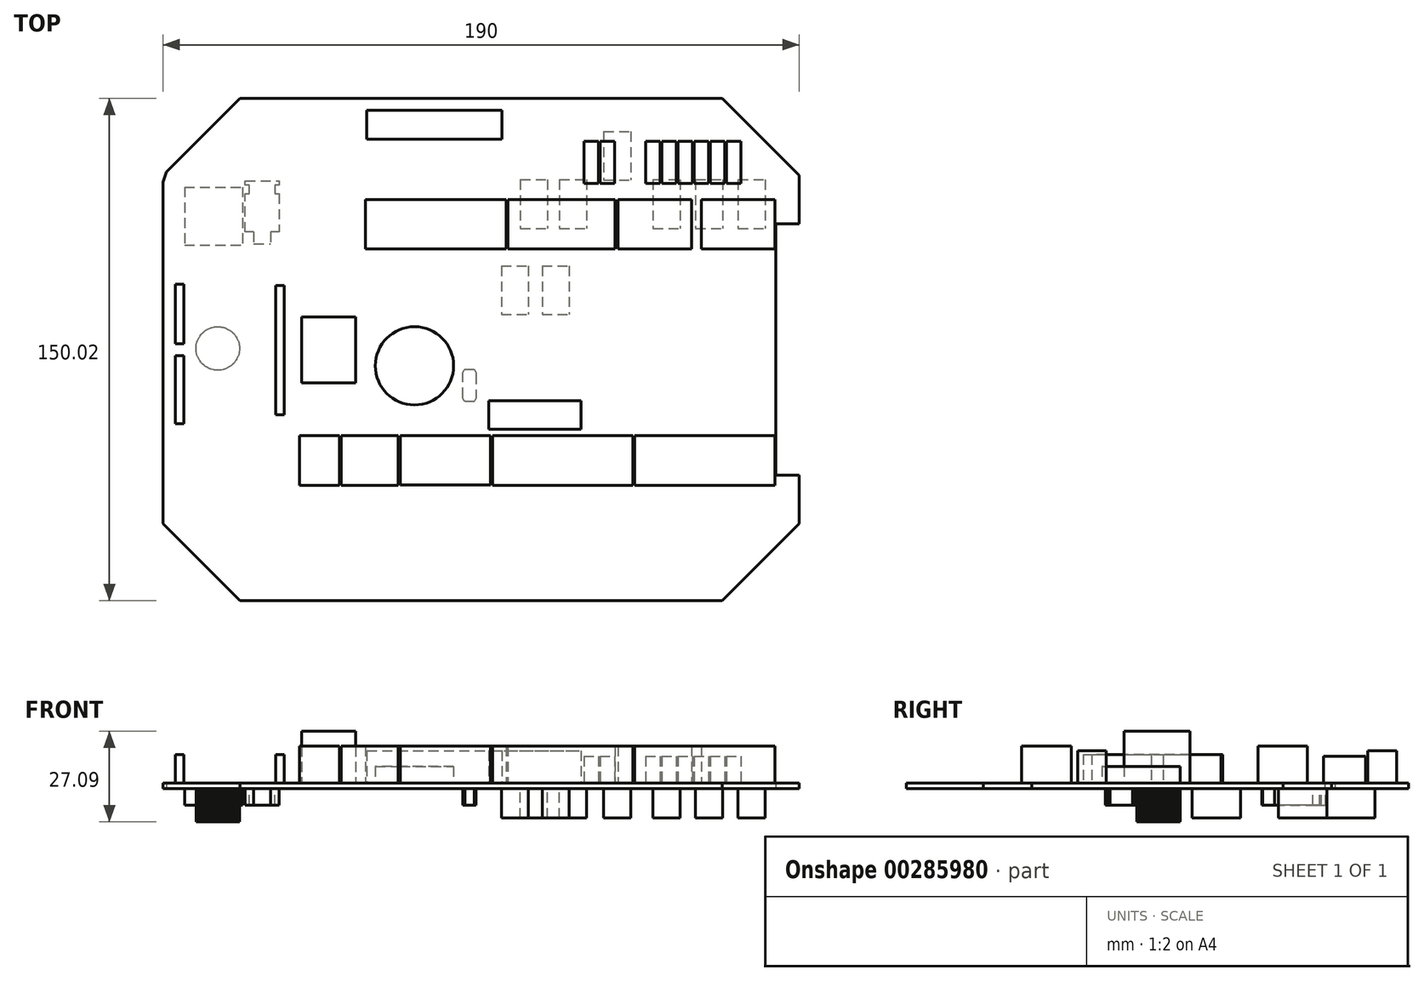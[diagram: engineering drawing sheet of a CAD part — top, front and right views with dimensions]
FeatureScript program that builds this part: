
annotation { "Feature Type Name" : "Feature", "Feature Type Description" : "" }
export const myFeature = defineFeature(function(context is Context, id is Id, definition is map)
    precondition{}
    {
        {
            var Q0;
            Q0=qCreatedBy(makeId("Top.planeOp"),FACE);
            var sketch = newSketch(context, id + "F0", { "sketchPlane" : qUnion([Q0])});
            skLineSegment(sketch, "E0", {"start": v(-92.96, -47) * mm, "end": v(-92.7, -46.96) * mm});
            skLineSegment(sketch, "E1", {"start": v(-92.7, -46.96) * mm, "end": v(-92.46, -46.91) * mm});
            skLineSegment(sketch, "E2", {"start": v(-92.46, -46.91) * mm, "end": v(-92.23, -46.81) * mm});
            skLineSegment(sketch, "E3", {"start": v(-92.23, -46.81) * mm, "end": v(-92.02, -46.69) * mm});
            skLineSegment(sketch, "E4", {"start": v(-92.02, -46.69) * mm, "end": v(-91.85, -46.5) * mm});
            skLineSegment(sketch, "E5", {"start": v(-91.85, -46.5) * mm, "end": v(-91.7, -46.33) * mm});
            skLineSegment(sketch, "E6", {"start": v(-91.7, -46.33) * mm, "end": v(-91.5, -45.87) * mm});
            skLineSegment(sketch, "E7", {"start": v(-91.5, -45.87) * mm, "end": v(-91.47, -45.62) * mm});
            skLineSegment(sketch, "E8", {"start": v(-91.47, -45.62) * mm, "end": v(-91.47, -45.36) * mm});
            skLineSegment(sketch, "E9", {"start": v(-91.47, -45.36) * mm, "end": v(-91.5, -45.14) * mm});
            skLineSegment(sketch, "E10", {"start": v(-91.5, -45.14) * mm, "end": v(-91.6, -44.88) * mm});
            skLineSegment(sketch, "E11", {"start": v(-91.6, -44.88) * mm, "end": v(-91.7, -44.68) * mm});
            skLineSegment(sketch, "E12", {"start": v(-91.7, -44.68) * mm, "end": v(-91.85, -44.5) * mm});
            skLineSegment(sketch, "E13", {"start": v(-91.85, -44.5) * mm, "end": v(-92.02, -44.32) * mm});
            skLineSegment(sketch, "E14", {"start": v(-92.02, -44.32) * mm, "end": v(-92.23, -44.17) * mm});
            skLineSegment(sketch, "E15", {"start": v(-92.23, -44.17) * mm, "end": v(-92.46, -44.1) * mm});
            skLineSegment(sketch, "E16", {"start": v(-92.46, -44.1) * mm, "end": v(-92.7, -44.02) * mm});
            skLineSegment(sketch, "E17", {"start": v(-92.7, -44.02) * mm, "end": v(-92.96, -44) * mm});
            skLineSegment(sketch, "E18", {"start": v(-92.68, 50.01) * mm, "end": v(-92.46, 50.09) * mm});
            skLineSegment(sketch, "E19", {"start": v(-92.46, 50.09) * mm, "end": v(-92.2, 50.2) * mm});
            skLineSegment(sketch, "E20", {"start": v(-92.2, 50.2) * mm, "end": v(-92, 50.37) * mm});
            skLineSegment(sketch, "E21", {"start": v(-92, 50.37) * mm, "end": v(-91.82, 50.52) * mm});
            skLineSegment(sketch, "E22", {"start": v(-91.82, 50.52) * mm, "end": v(-91.64, 50.75) * mm});
            skLineSegment(sketch, "E23", {"start": v(-91.64, 50.75) * mm, "end": v(-91.54, 50.98) * mm});
            skLineSegment(sketch, "E24", {"start": v(-91.54, 50.98) * mm, "end": v(-91.47, 51.23) * mm});
            skLineSegment(sketch, "E25", {"start": v(-91.47, 51.23) * mm, "end": v(-91.47, 51.74) * mm});
            skLineSegment(sketch, "E26", {"start": v(-91.47, 51.74) * mm, "end": v(-91.54, 52) * mm});
            skLineSegment(sketch, "E27", {"start": v(-91.54, 52) * mm, "end": v(-91.64, 52.25) * mm});
            skLineSegment(sketch, "E28", {"start": v(-91.64, 52.25) * mm, "end": v(-91.8, 52.45) * mm});
            skLineSegment(sketch, "E29", {"start": v(-91.8, 52.45) * mm, "end": v(-91.97, 52.65) * mm});
            skLineSegment(sketch, "E30", {"start": v(-91.97, 52.65) * mm, "end": v(-92.18, 52.78) * mm});
            skLineSegment(sketch, "E31", {"start": v(-92.18, 52.78) * mm, "end": v(-92.43, 52.9) * mm});
            skLineSegment(sketch, "E32", {"start": v(-92.43, 52.9) * mm, "end": v(-92.68, 52.98) * mm});
            skLineSegment(sketch, "E33", {"start": v(88.01, -37.5) * mm, "end": v(88.01, 37.5) * mm});
            skLineSegment(sketch, "E34", {"start": v(-95, -47) * mm, "end": v(-92.96, -47) * mm});
            skLineSegment(sketch, "E35", {"start": v(-95, 50.01) * mm, "end": v(-92.68, 50.01) * mm});
            skLineSegment(sketch, "E36", {"start": v(-72, 75) * mm, "end": v(72, 75) * mm});
            skLineSegment(sketch, "E37", {"start": v(-72, -75) * mm, "end": v(72, -75) * mm});
            skLineSegment(sketch, "E38", {"start": v(-95, -52) * mm, "end": v(-72, -75) * mm});
            skLineSegment(sketch, "E39", {"start": v(95, 37.5) * mm, "end": v(95, 52) * mm});
            skLineSegment(sketch, "E40", {"start": v(95, -52) * mm, "end": v(95, -37.5) * mm});
            skLineSegment(sketch, "E41", {"start": v(72, 75) * mm, "end": v(95, 52) * mm});
            skLineSegment(sketch, "E42", {"start": v(72, -75) * mm, "end": v(95, -52) * mm});
            skLineSegment(sketch, "E43", {"start": v(88.01, 37.5) * mm, "end": v(95, 37.5) * mm});
            skLineSegment(sketch, "E44", {"start": v(88.01, -37.5) * mm, "end": v(95, -37.5) * mm});
            skLineSegment(sketch, "E45", {"start": v(-93.2, 52.98) * mm, "end": v(-92.68, 52.98) * mm});
            skLineSegment(sketch, "E46", {"start": v(-94, 53) * mm, "end": v(-72, 75) * mm});
            skLineSegment(sketch, "E47", {"start": v(-94, 53) * mm, "end": v(-93.22, 53) * mm});
            skLineSegment(sketch, "E48", {"start": v(-95, -44) * mm, "end": v(-92.96, -44) * mm});
            skLineSegment(sketch, "E49", {"start": v(-95, -52) * mm, "end": v(-95, 50.01) * mm});
            skLineSegment(sketch, "E50", {"start": v(-95, 50.01) * mm, "end": v(-94, 53) * mm});
            skSolve(sketch);
        }
        {
            var Q0;
            Q0 = qSketchRegion(id + "F0", true);
            extrude(context, id + "F1", {"entities" : qUnion([Q0]), "depth" : 1.6 * mm});
        }
        {
            var Q0;
            Q0=makeQuery(id+"F1.opExtrude","CAP_FACE",FACE,{"disambiguationData":[OSD([sQuery(id+"F0.wireOp",EDGE,"E33"),sQuery(id+"F0.wireOp",EDGE,"E36"),sQuery(id+"F0.wireOp",EDGE,"E37"),sQuery(id+"F0.wireOp",EDGE,"E38"),sQuery(id+"F0.wireOp",EDGE,"E39"),sQuery(id+"F0.wireOp",EDGE,"E40"),sQuery(id+"F0.wireOp",EDGE,"E41"),sQuery(id+"F0.wireOp",EDGE,"E42"),sQuery(id+"F0.wireOp",EDGE,"E43"),sQuery(id+"F0.wireOp",EDGE,"E44"),sQuery(id+"F0.wireOp",EDGE,"E46"),sQuery(id+"F0.wireOp",EDGE,"E49"),sQuery(id+"F0.wireOp",EDGE,"E50")])],"isStart":false});
            var sketch = newSketch(context, id + "F2", { "sketchPlane" : qUnion([Q0])});
            skLineSegment(sketch, "E51", {"start": v(-92.96, -47) * mm, "end": v(-92.7, -46.96) * mm});
            skLineSegment(sketch, "E52", {"start": v(-92.7, -46.96) * mm, "end": v(-92.46, -46.91) * mm});
            skLineSegment(sketch, "E53", {"start": v(-92.46, -46.91) * mm, "end": v(-92.23, -46.81) * mm});
            skLineSegment(sketch, "E54", {"start": v(-92.23, -46.81) * mm, "end": v(-92.02, -46.69) * mm});
            skLineSegment(sketch, "E55", {"start": v(-92.02, -46.69) * mm, "end": v(-91.85, -46.5) * mm});
            skLineSegment(sketch, "E56", {"start": v(-91.85, -46.5) * mm, "end": v(-91.7, -46.33) * mm});
            skLineSegment(sketch, "E57", {"start": v(-91.7, -46.33) * mm, "end": v(-91.6, -46.1) * mm});
            skLineSegment(sketch, "E58", {"start": v(-91.6, -46.1) * mm, "end": v(-91.5, -45.87) * mm});
            skLineSegment(sketch, "E59", {"start": v(-91.5, -45.87) * mm, "end": v(-91.47, -45.62) * mm});
            skLineSegment(sketch, "E60", {"start": v(-91.47, -45.62) * mm, "end": v(-91.47, -45.36) * mm});
            skLineSegment(sketch, "E61", {"start": v(-91.47, -45.36) * mm, "end": v(-91.5, -45.14) * mm});
            skLineSegment(sketch, "E62", {"start": v(-91.5, -45.14) * mm, "end": v(-91.6, -44.88) * mm});
            skLineSegment(sketch, "E63", {"start": v(-91.6, -44.88) * mm, "end": v(-91.7, -44.68) * mm});
            skLineSegment(sketch, "E64", {"start": v(-91.7, -44.68) * mm, "end": v(-91.85, -44.5) * mm});
            skLineSegment(sketch, "E65", {"start": v(-91.85, -44.5) * mm, "end": v(-92.02, -44.32) * mm});
            skLineSegment(sketch, "E66", {"start": v(-92.02, -44.32) * mm, "end": v(-92.23, -44.17) * mm});
            skLineSegment(sketch, "E67", {"start": v(-92.23, -44.17) * mm, "end": v(-92.46, -44.1) * mm});
            skLineSegment(sketch, "E68", {"start": v(-92.46, -44.1) * mm, "end": v(-92.7, -44.02) * mm});
            skLineSegment(sketch, "E69", {"start": v(-92.7, -44.02) * mm, "end": v(-92.96, -44) * mm});
            skLineSegment(sketch, "E70", {"start": v(-92.96, 50.01) * mm, "end": v(-92.68, 50.01) * mm});
            skLineSegment(sketch, "E71", {"start": v(-92.68, 50.01) * mm, "end": v(-92.46, 50.09) * mm});
            skLineSegment(sketch, "E72", {"start": v(-92.46, 50.09) * mm, "end": v(-92.2, 50.2) * mm});
            skLineSegment(sketch, "E73", {"start": v(-92.2, 50.2) * mm, "end": v(-92, 50.37) * mm});
            skLineSegment(sketch, "E74", {"start": v(-92, 50.37) * mm, "end": v(-91.82, 50.52) * mm});
            skLineSegment(sketch, "E75", {"start": v(-91.82, 50.52) * mm, "end": v(-91.64, 50.75) * mm});
            skLineSegment(sketch, "E76", {"start": v(-91.64, 50.75) * mm, "end": v(-91.54, 50.98) * mm});
            skLineSegment(sketch, "E77", {"start": v(-91.54, 50.98) * mm, "end": v(-91.47, 51.23) * mm});
            skLineSegment(sketch, "E78", {"start": v(-91.47, 51.23) * mm, "end": v(-91.47, 51.49) * mm});
            skLineSegment(sketch, "E79", {"start": v(-91.47, 51.49) * mm, "end": v(-91.47, 51.74) * mm});
            skLineSegment(sketch, "E80", {"start": v(-91.47, 51.74) * mm, "end": v(-91.54, 52) * mm});
            skLineSegment(sketch, "E81", {"start": v(-91.54, 52) * mm, "end": v(-91.64, 52.25) * mm});
            skLineSegment(sketch, "E82", {"start": v(-91.64, 52.25) * mm, "end": v(-91.8, 52.45) * mm});
            skLineSegment(sketch, "E83", {"start": v(-91.8, 52.45) * mm, "end": v(-91.97, 52.65) * mm});
            skLineSegment(sketch, "E84", {"start": v(-91.97, 52.65) * mm, "end": v(-92.18, 52.78) * mm});
            skLineSegment(sketch, "E85", {"start": v(-92.18, 52.78) * mm, "end": v(-92.43, 52.9) * mm});
            skLineSegment(sketch, "E86", {"start": v(-92.43, 52.9) * mm, "end": v(-92.68, 52.98) * mm});
            skLineSegment(sketch, "E87", {"start": v(88.01, -37.5) * mm, "end": v(88.01, 37.5) * mm});
            skLineSegment(sketch, "E88", {"start": v(-95, -44) * mm, "end": v(-95, 50.01) * mm});
            skLineSegment(sketch, "E89", {"start": v(-95, -52) * mm, "end": v(-95, -47) * mm});
            skLineSegment(sketch, "E90", {"start": v(-95, -44) * mm, "end": v(-92.96, -44) * mm});
            skLineSegment(sketch, "E91", {"start": v(-95, -47) * mm, "end": v(-92.96, -47) * mm});
            skLineSegment(sketch, "E92", {"start": v(-95, 50.01) * mm, "end": v(-92.96, 50.01) * mm});
            skLineSegment(sketch, "E93", {"start": v(-72, 75) * mm, "end": v(72, 75) * mm});
            skLineSegment(sketch, "E94", {"start": v(-72, -75) * mm, "end": v(72, -75) * mm});
            skLineSegment(sketch, "E95", {"start": v(-95, -52) * mm, "end": v(-72, -75) * mm});
            skLineSegment(sketch, "E96", {"start": v(95, 37.5) * mm, "end": v(95, 52) * mm});
            skLineSegment(sketch, "E97", {"start": v(95, -52) * mm, "end": v(95, -37.5) * mm});
            skLineSegment(sketch, "E98", {"start": v(72, 75) * mm, "end": v(95, 52) * mm});
            skLineSegment(sketch, "E99", {"start": v(72, -75) * mm, "end": v(95, -52) * mm});
            skLineSegment(sketch, "E100", {"start": v(88.01, 37.5) * mm, "end": v(95, 37.5) * mm});
            skLineSegment(sketch, "E101", {"start": v(88.01, -37.5) * mm, "end": v(95, -37.5) * mm});
            skLineSegment(sketch, "E102", {"start": v(-93.2, 52.98) * mm, "end": v(-92.68, 52.98) * mm});
            skLineSegment(sketch, "E103", {"start": v(-94, 53) * mm, "end": v(-72, 75) * mm});
            skLineSegment(sketch, "E104", {"start": v(-94, 53) * mm, "end": v(-93.22, 53) * mm});
            skLineSegment(sketch, "E105", {"start": v(-34.09, 62.84) * mm, "end": v(-34.09, 71.42) * mm});
            skLineSegment(sketch, "E106", {"start": v(6.25, 62.84) * mm, "end": v(6.25, 71.42) * mm});
            skLineSegment(sketch, "E107", {"start": v(-34.09, 71.42) * mm, "end": v(-30.7, 71.42) * mm});
            skLineSegment(sketch, "E108", {"start": v(-34.09, 62.84) * mm, "end": v(-30.7, 62.84) * mm});
            skLineSegment(sketch, "E109", {"start": v(2.82, 71.42) * mm, "end": v(6.25, 71.42) * mm});
            skLineSegment(sketch, "E110", {"start": v(2.84, 62.84) * mm, "end": v(6.25, 62.84) * mm});
            skLineSegment(sketch, "E111", {"start": v(73.28, 49.58) * mm, "end": v(73.28, 62.18) * mm});
            skLineSegment(sketch, "E112", {"start": v(77.57, 49.58) * mm, "end": v(77.57, 62.18) * mm});
            skLineSegment(sketch, "E113", {"start": v(73.28, 49.58) * mm, "end": v(77.57, 49.58) * mm});
            skLineSegment(sketch, "E114", {"start": v(73.28, 62.18) * mm, "end": v(77.57, 62.18) * mm});
            skLineSegment(sketch, "E115", {"start": v(68.45, 49.58) * mm, "end": v(68.45, 62.18) * mm});
            skLineSegment(sketch, "E116", {"start": v(72.75, 49.58) * mm, "end": v(72.75, 62.18) * mm});
            skLineSegment(sketch, "E117", {"start": v(68.45, 49.58) * mm, "end": v(72.75, 49.58) * mm});
            skLineSegment(sketch, "E118", {"start": v(68.45, 62.18) * mm, "end": v(72.75, 62.18) * mm});
            skLineSegment(sketch, "E119", {"start": v(63.63, 49.58) * mm, "end": v(63.63, 62.18) * mm});
            skLineSegment(sketch, "E120", {"start": v(67.92, 49.58) * mm, "end": v(67.92, 62.18) * mm});
            skLineSegment(sketch, "E121", {"start": v(63.63, 49.58) * mm, "end": v(67.92, 49.58) * mm});
            skLineSegment(sketch, "E122", {"start": v(63.63, 62.18) * mm, "end": v(67.92, 62.18) * mm});
            skLineSegment(sketch, "E123", {"start": v(58.8, 49.58) * mm, "end": v(58.8, 62.18) * mm});
            skLineSegment(sketch, "E124", {"start": v(63.1, 49.58) * mm, "end": v(63.1, 62.18) * mm});
            skLineSegment(sketch, "E125", {"start": v(58.8, 49.58) * mm, "end": v(63.1, 49.58) * mm});
            skLineSegment(sketch, "E126", {"start": v(58.8, 62.18) * mm, "end": v(63.1, 62.18) * mm});
            skLineSegment(sketch, "E127", {"start": v(53.98, 49.58) * mm, "end": v(53.98, 62.18) * mm});
            skLineSegment(sketch, "E128", {"start": v(58.27, 49.58) * mm, "end": v(58.27, 62.18) * mm});
            skLineSegment(sketch, "E129", {"start": v(53.98, 49.58) * mm, "end": v(58.27, 49.58) * mm});
            skLineSegment(sketch, "E130", {"start": v(53.98, 62.18) * mm, "end": v(58.27, 62.18) * mm});
            skLineSegment(sketch, "E131", {"start": v(49.15, 49.58) * mm, "end": v(49.15, 62.18) * mm});
            skLineSegment(sketch, "E132", {"start": v(53.44, 49.58) * mm, "end": v(53.44, 62.18) * mm});
            skLineSegment(sketch, "E133", {"start": v(49.15, 49.58) * mm, "end": v(53.44, 49.58) * mm});
            skLineSegment(sketch, "E134", {"start": v(49.15, 62.18) * mm, "end": v(53.44, 62.18) * mm});
            skLineSegment(sketch, "E135", {"start": v(35.56, 49.58) * mm, "end": v(35.56, 62.18) * mm});
            skLineSegment(sketch, "E136", {"start": v(39.85, 49.58) * mm, "end": v(39.85, 62.18) * mm});
            skLineSegment(sketch, "E137", {"start": v(35.56, 49.58) * mm, "end": v(39.85, 49.58) * mm});
            skLineSegment(sketch, "E138", {"start": v(35.56, 62.18) * mm, "end": v(39.85, 62.18) * mm});
            skLineSegment(sketch, "E139", {"start": v(30.73, 49.58) * mm, "end": v(30.73, 62.18) * mm});
            skLineSegment(sketch, "E140", {"start": v(35.03, 49.58) * mm, "end": v(35.03, 62.18) * mm});
            skLineSegment(sketch, "E141", {"start": v(30.73, 49.58) * mm, "end": v(35.03, 49.58) * mm});
            skLineSegment(sketch, "E142", {"start": v(30.73, 62.18) * mm, "end": v(35.03, 62.18) * mm});
            skLineSegment(sketch, "E143", {"start": v(45.82, -40.54) * mm, "end": v(45.82, -25.73) * mm});
            skLineSegment(sketch, "E144", {"start": v(45.82, -25.73) * mm, "end": v(87.83, -25.73) * mm});
            skLineSegment(sketch, "E145", {"start": v(87.83, -25.73) * mm, "end": v(87.83, -40.54) * mm});
            skLineSegment(sketch, "E146", {"start": v(87.83, -40.54) * mm, "end": v(45.82, -40.54) * mm});
            skLineSegment(sketch, "E147", {"start": v(45.82, -34.34) * mm, "end": v(87.83, -34.34) * mm});
            skLineSegment(sketch, "E148", {"start": v(-54.25, -40.54) * mm, "end": v(-54.25, -25.73) * mm});
            skLineSegment(sketch, "E149", {"start": v(-54.25, -25.73) * mm, "end": v(-42.27, -25.73) * mm});
            skLineSegment(sketch, "E150", {"start": v(-54.25, -40.54) * mm, "end": v(-42.27, -40.54) * mm});
            skLineSegment(sketch, "E151", {"start": v(-42.27, -40.54) * mm, "end": v(-42.27, -25.73) * mm});
            skLineSegment(sketch, "E152", {"start": v(-54.25, -34.34) * mm, "end": v(-42.34, -34.34) * mm});
            skLineSegment(sketch, "E153", {"start": v(-41.7, -40.54) * mm, "end": v(-41.7, -25.73) * mm});
            skLineSegment(sketch, "E154", {"start": v(-41.7, -25.73) * mm, "end": v(-24.69, -25.73) * mm});
            skLineSegment(sketch, "E155", {"start": v(-41.7, -40.54) * mm, "end": v(-24.69, -40.54) * mm});
            skLineSegment(sketch, "E156", {"start": v(-24.69, -40.54) * mm, "end": v(-24.69, -25.73) * mm});
            skLineSegment(sketch, "E157", {"start": v(-41.66, -34.34) * mm, "end": v(-24.76, -34.34) * mm});
            skLineSegment(sketch, "E158", {"start": v(87.83, 30) * mm, "end": v(87.83, 44.8) * mm});
            skLineSegment(sketch, "E159", {"start": v(65.84, 30) * mm, "end": v(87.83, 30) * mm});
            skLineSegment(sketch, "E160", {"start": v(65.84, 44.8) * mm, "end": v(87.83, 44.8) * mm});
            skLineSegment(sketch, "E161", {"start": v(65.84, 30) * mm, "end": v(65.84, 44.8) * mm});
            skLineSegment(sketch, "E162", {"start": v(65.84, 36.2) * mm, "end": v(87.83, 36.2) * mm});
            skLineSegment(sketch, "E163", {"start": v(62.94, 30) * mm, "end": v(62.94, 44.8) * mm});
            skLineSegment(sketch, "E164", {"start": v(40.92, 30) * mm, "end": v(62.94, 30) * mm});
            skLineSegment(sketch, "E165", {"start": v(40.92, 44.8) * mm, "end": v(62.94, 44.8) * mm});
            skLineSegment(sketch, "E166", {"start": v(40.92, 30) * mm, "end": v(40.92, 44.8) * mm});
            skLineSegment(sketch, "E167", {"start": v(40.92, 36.2) * mm, "end": v(62.94, 36.2) * mm});
            skLineSegment(sketch, "E168", {"start": v(-61.3, 19.05) * mm, "end": v(-58.75, 19.05) * mm});
            skLineSegment(sketch, "E169", {"start": v(-58.75, 19.05) * mm, "end": v(-58.75, -19.56) * mm});
            skLineSegment(sketch, "E170", {"start": v(-58.75, -19.56) * mm, "end": v(-61.3, -19.56) * mm});
            skLineSegment(sketch, "E171", {"start": v(-61.3, -19.56) * mm, "end": v(-61.3, 19.05) * mm});
            skLineSegment(sketch, "E172", {"start": v(-88.75, 1.75) * mm, "end": v(-88.75, 19.53) * mm});
            skLineSegment(sketch, "E173", {"start": v(-91.29, 1.75) * mm, "end": v(-88.75, 1.75) * mm});
            skLineSegment(sketch, "E174", {"start": v(-91.29, 1.75) * mm, "end": v(-91.29, 19.53) * mm});
            skLineSegment(sketch, "E175", {"start": v(-91.29, 19.53) * mm, "end": v(-88.75, 19.53) * mm});
            skLineSegment(sketch, "E176", {"start": v(-88.75, -22.15) * mm, "end": v(-88.75, -1.83) * mm});
            skLineSegment(sketch, "E177", {"start": v(-91.29, -22.15) * mm, "end": v(-88.75, -22.15) * mm});
            skLineSegment(sketch, "E178", {"start": v(-91.29, -22.15) * mm, "end": v(-91.29, -1.83) * mm});
            skLineSegment(sketch, "E179", {"start": v(-91.29, -1.83) * mm, "end": v(-88.75, -1.83) * mm});
            skLineSegment(sketch, "E180", {"start": v(3.4, -34.34) * mm, "end": v(45.39, -34.34) * mm});
            skLineSegment(sketch, "E181", {"start": v(3.4, -40.54) * mm, "end": v(45.39, -40.54) * mm});
            skLineSegment(sketch, "E182", {"start": v(45.39, -40.54) * mm, "end": v(45.39, -25.73) * mm});
            skLineSegment(sketch, "E183", {"start": v(45.39, -25.73) * mm, "end": v(3.4, -25.73) * mm});
            skLineSegment(sketch, "E184", {"start": v(3.4, -25.73) * mm, "end": v(3.4, -40.54) * mm});
            skLineSegment(sketch, "E185", {"start": v(2.26, -23.85) * mm, "end": v(2.26, -15.27) * mm});
            skLineSegment(sketch, "E186", {"start": v(29.92, -23.85) * mm, "end": v(29.92, -15.27) * mm});
            skLineSegment(sketch, "E187", {"start": v(29.92, -15.27) * mm, "end": v(26.75, -15.27) * mm});
            skLineSegment(sketch, "E188", {"start": v(26.77, -23.85) * mm, "end": v(29.92, -23.85) * mm});
            skLineSegment(sketch, "E189", {"start": v(2.26, -15.27) * mm, "end": v(5.66, -15.27) * mm});
            skLineSegment(sketch, "E190", {"start": v(2.26, -23.85) * mm, "end": v(5.54, -23.85) * mm});
            skLineSegment(sketch, "E191", {"start": v(-24.13, -40.51) * mm, "end": v(-24.13, -25.73) * mm});
            skLineSegment(sketch, "E192", {"start": v(-24.13, -25.73) * mm, "end": v(2.87, -25.73) * mm});
            skLineSegment(sketch, "E193", {"start": v(-24.13, -40.51) * mm, "end": v(2.87, -40.51) * mm});
            skLineSegment(sketch, "E194", {"start": v(2.87, -40.51) * mm, "end": v(2.87, -25.73) * mm});
            skLineSegment(sketch, "E195", {"start": v(-24.13, -34.32) * mm, "end": v(2.87, -34.32) * mm});
            skLineSegment(sketch, "E196", {"start": v(-53.57, 9.75) * mm, "end": v(-37.44, 9.75) * mm});
            skLineSegment(sketch, "E197", {"start": v(-53.57, -9.98) * mm, "end": v(-53.57, 9.75) * mm});
            skLineSegment(sketch, "E198", {"start": v(-53.57, -9.98) * mm, "end": v(-37.44, -9.96) * mm});
            skLineSegment(sketch, "E199", {"start": v(-37.44, -9.96) * mm, "end": v(-37.44, 9.75) * mm});
            skLineSegment(sketch, "E200", {"start": v(7.98, 30) * mm, "end": v(7.98, 44.8) * mm});
            skLineSegment(sketch, "E201", {"start": v(7.98, 44.8) * mm, "end": v(40, 44.8) * mm});
            skLineSegment(sketch, "E202", {"start": v(40, 44.8) * mm, "end": v(40, 30) * mm});
            skLineSegment(sketch, "E203", {"start": v(40, 30) * mm, "end": v(7.98, 30) * mm});
            skLineSegment(sketch, "E204", {"start": v(7.98, 36.2) * mm, "end": v(40, 36.2) * mm});
            skLineSegment(sketch, "E205", {"start": v(-34.5, 30) * mm, "end": v(-34.5, 44.8) * mm});
            skLineSegment(sketch, "E206", {"start": v(-34.5, 44.8) * mm, "end": v(7.5, 44.8) * mm});
            skLineSegment(sketch, "E207", {"start": v(7.5, 44.8) * mm, "end": v(7.5, 30) * mm});
            skLineSegment(sketch, "E208", {"start": v(7.5, 30) * mm, "end": v(-34.5, 30) * mm});
            skLineSegment(sketch, "E209", {"start": v(-34.5, 36.2) * mm, "end": v(7.5, 36.2) * mm});
            skCircle(sketch, "E210", {"center": v(-19.87, -4.9) * mm, "radius": 11.69 * mm});
            skLineSegment(sketch, "E211", {"start": v(5.66, -15.27) * mm, "end": v(26.75, -15.27) * mm});
            skLineSegment(sketch, "E212", {"start": v(5.54, -23.85) * mm, "end": v(26.77, -23.85) * mm});
            skLineSegment(sketch, "E213", {"start": v(-30.7, 71.42) * mm, "end": v(2.82, 71.42) * mm});
            skLineSegment(sketch, "E214", {"start": v(-30.7, 62.84) * mm, "end": v(2.84, 62.84) * mm});
            skSolve(sketch);
        }
        {
            var Q0;
            {var subQ0=sQuery(id+"F2.wireOp",EDGE,"E206");Q0=makeQuery(id+"F2.imprint","IMPRINT",FACE,{"disambiguationData":[TD([[makeQuery(id+"F2.imprint","IMPRINT",EDGE,{"derivedFrom":subQ0}),-1.0]])]});}
            var Q1;
            {var subQ0=sQuery(id+"F2.wireOp",EDGE,"E208");Q1=makeQuery(id+"F2.imprint","IMPRINT",FACE,{"disambiguationData":[TD([[makeQuery(id+"F2.imprint","IMPRINT",EDGE,{"derivedFrom":subQ0}),-1.0]])]});}
            var Q2;
            {var subQ0=sQuery(id+"F2.wireOp",EDGE,"E201");Q2=makeQuery(id+"F2.imprint","IMPRINT",FACE,{"disambiguationData":[TD([[makeQuery(id+"F2.imprint","IMPRINT",EDGE,{"derivedFrom":subQ0}),-1.0]])]});}
            var Q3;
            {var subQ0=sQuery(id+"F2.wireOp",EDGE,"E203");Q3=makeQuery(id+"F2.imprint","IMPRINT",FACE,{"disambiguationData":[TD([[makeQuery(id+"F2.imprint","IMPRINT",EDGE,{"derivedFrom":subQ0}),-1.0]])]});}
            var Q4;
            {var subQ0=sQuery(id+"F2.wireOp",EDGE,"E165");Q4=makeQuery(id+"F2.imprint","IMPRINT",FACE,{"disambiguationData":[TD([[makeQuery(id+"F2.imprint","IMPRINT",EDGE,{"derivedFrom":subQ0}),-1.0]])]});}
            var Q5;
            {var subQ0=sQuery(id+"F2.wireOp",EDGE,"E164");Q5=makeQuery(id+"F2.imprint","IMPRINT",FACE,{"disambiguationData":[TD([[makeQuery(id+"F2.imprint","IMPRINT",EDGE,{"derivedFrom":subQ0}),1.0]])]});}
            var Q6;
            {var subQ0=sQuery(id+"F2.wireOp",EDGE,"E160");Q6=makeQuery(id+"F2.imprint","IMPRINT",FACE,{"disambiguationData":[TD([[makeQuery(id+"F2.imprint","IMPRINT",EDGE,{"derivedFrom":subQ0}),-1.0]])]});}
            var Q7;
            {var subQ0=sQuery(id+"F2.wireOp",EDGE,"E144");Q7=makeQuery(id+"F2.imprint","IMPRINT",FACE,{"disambiguationData":[TD([[makeQuery(id+"F2.imprint","IMPRINT",EDGE,{"derivedFrom":subQ0}),-1.0]])]});}
            var Q8;
            {var subQ0=sQuery(id+"F2.wireOp",EDGE,"E146");Q8=makeQuery(id+"F2.imprint","IMPRINT",FACE,{"disambiguationData":[TD([[makeQuery(id+"F2.imprint","IMPRINT",EDGE,{"derivedFrom":subQ0}),-1.0]])]});}
            var Q9;
            {var subQ0=sQuery(id+"F2.wireOp",EDGE,"E180");Q9=makeQuery(id+"F2.imprint","IMPRINT",FACE,{"disambiguationData":[TD([[makeQuery(id+"F2.imprint","IMPRINT",EDGE,{"derivedFrom":subQ0}),1.0]])]});}
            var Q10;
            {var subQ0=sQuery(id+"F2.wireOp",EDGE,"E180");Q10=makeQuery(id+"F2.imprint","IMPRINT",FACE,{"disambiguationData":[TD([[makeQuery(id+"F2.imprint","IMPRINT",EDGE,{"derivedFrom":subQ0}),-1.0]])]});}
            var Q11;
            {var subQ0=sQuery(id+"F2.wireOp",EDGE,"E192");Q11=makeQuery(id+"F2.imprint","IMPRINT",FACE,{"disambiguationData":[TD([[makeQuery(id+"F2.imprint","IMPRINT",EDGE,{"derivedFrom":subQ0}),-1.0]])]});}
            var Q12;
            {var subQ0=sQuery(id+"F2.wireOp",EDGE,"E193");Q12=makeQuery(id+"F2.imprint","IMPRINT",FACE,{"disambiguationData":[TD([[makeQuery(id+"F2.imprint","IMPRINT",EDGE,{"derivedFrom":subQ0}),1.0]])]});}
            var Q13;
            {var subQ1=sQuery(id+"F2.wireOp",EDGE,"E149");Q13=makeQuery(id+"F2.imprint","IMPRINT",FACE,{"disambiguationData":[TD([[makeQuery(id+"F2.imprint","IMPRINT",EDGE,{"derivedFrom":subQ1}),-1.0]])]});}
            var Q14;
            Q14=makeQuery(id+"F2.imprint","IMPRINT",FACE,{"disambiguationData":[TD([[makeQuery(id+"F2.imprint","IMPRINT",EDGE,{"derivedFrom":sQuery(id+"F2.wireOp",EDGE,"E153")}),-1.0]])]});
            var Q15;
            {var subQ0=sQuery(id+"F2.wireOp",EDGE,"E159");Q15=makeQuery(id+"F2.imprint","IMPRINT",FACE,{"disambiguationData":[TD([[makeQuery(id+"F2.imprint","IMPRINT",EDGE,{"derivedFrom":subQ0}),1.0]])]});}
            extrude(context, id + "F3", {"entities" : qUnion([Q0, Q1, Q2, Q3, Q4, Q5, Q6, Q7, Q8, Q9, Q10, Q11, Q12, Q13, Q14, Q15]), "operationType" : NewBodyOperationType.ADD, "depth" : 11 * mm});
        }
        {
            var Q0;
            Q0=makeQuery(id+"F2.imprint","IMPRINT",FACE,{"disambiguationData":[TD([[makeQuery(id+"F2.imprint","IMPRINT",EDGE,{"derivedFrom":sQuery(id+"F2.wireOp",EDGE,"E210")}),1.0]])]});
            var Q1;
            Q1=sQuery(id+"F2.wireOp",EDGE,"E210");
            extrude(context, id + "F4", {"entities" : qUnion([Q0]), "operationType" : NewBodyOperationType.ADD, "surfaceEntities" : qUnion([Q1]), "depth" : 4.95 * mm});
        }
        {
            var Q0;
            Q0=makeQuery(id+"F2.imprint","IMPRINT",FACE,{"disambiguationData":[TD([[makeQuery(id+"F2.imprint","IMPRINT",EDGE,{"derivedFrom":sQuery(id+"F2.wireOp",EDGE,"E196")}),-1.0]])]});
            extrude(context, id + "F5", {"entities" : qUnion([Q0]), "operationType" : NewBodyOperationType.ADD, "depth" : 15.5 * mm});
        }
        {
            var Q0;
            Q0=makeQuery(id+"F2.imprint","IMPRINT",FACE,{"disambiguationData":[TD([[makeQuery(id+"F2.imprint","IMPRINT",EDGE,{"derivedFrom":sQuery(id+"F2.wireOp",EDGE,"E139")}),-1.0]])]});
            var Q1;
            Q1=makeQuery(id+"F2.imprint","IMPRINT",FACE,{"disambiguationData":[TD([[makeQuery(id+"F2.imprint","IMPRINT",EDGE,{"derivedFrom":sQuery(id+"F2.wireOp",EDGE,"E135")}),-1.0]])]});
            var Q2;
            Q2=makeQuery(id+"F2.imprint","IMPRINT",FACE,{"disambiguationData":[TD([[makeQuery(id+"F2.imprint","IMPRINT",EDGE,{"derivedFrom":sQuery(id+"F2.wireOp",EDGE,"E131")}),-1.0]])]});
            var Q3;
            Q3=makeQuery(id+"F2.imprint","IMPRINT",FACE,{"disambiguationData":[TD([[makeQuery(id+"F2.imprint","IMPRINT",EDGE,{"derivedFrom":sQuery(id+"F2.wireOp",EDGE,"E127")}),-1.0]])]});
            var Q4;
            Q4=makeQuery(id+"F2.imprint","IMPRINT",FACE,{"disambiguationData":[TD([[makeQuery(id+"F2.imprint","IMPRINT",EDGE,{"derivedFrom":sQuery(id+"F2.wireOp",EDGE,"E123")}),-1.0]])]});
            var Q5;
            Q5=makeQuery(id+"F2.imprint","IMPRINT",FACE,{"disambiguationData":[TD([[makeQuery(id+"F2.imprint","IMPRINT",EDGE,{"derivedFrom":sQuery(id+"F2.wireOp",EDGE,"E119")}),-1.0]])]});
            var Q6;
            Q6=makeQuery(id+"F2.imprint","IMPRINT",FACE,{"disambiguationData":[TD([[makeQuery(id+"F2.imprint","IMPRINT",EDGE,{"derivedFrom":sQuery(id+"F2.wireOp",EDGE,"E115")}),-1.0]])]});
            var Q7;
            Q7=makeQuery(id+"F2.imprint","IMPRINT",FACE,{"disambiguationData":[TD([[makeQuery(id+"F2.imprint","IMPRINT",EDGE,{"derivedFrom":sQuery(id+"F2.wireOp",EDGE,"E111")}),-1.0]])]});
            extrude(context, id + "F6", {"entities" : qUnion([Q0, Q1, Q2, Q3, Q4, Q5, Q6, Q7]), "operationType" : NewBodyOperationType.ADD, "depth" : 8 * mm});
        }
        {
            var Q0;
            Q0=makeQuery(id+"F2.imprint","IMPRINT",FACE,{"disambiguationData":[TD([[makeQuery(id+"F2.imprint","IMPRINT",EDGE,{"derivedFrom":sQuery(id+"F2.wireOp",EDGE,"E105")}),-1.0]])]});
            var Q1;
            Q1=makeQuery(id+"F2.imprint","IMPRINT",FACE,{"disambiguationData":[TD([[makeQuery(id+"F2.imprint","IMPRINT",EDGE,{"derivedFrom":sQuery(id+"F2.wireOp",EDGE,"E185")}),-1.0]])]});
            extrude(context, id + "F7", {"entities" : qUnion([Q0, Q1]), "operationType" : NewBodyOperationType.ADD, "depth" : 9.65 * mm});
        }
        {
            var Q0;
            Q0=makeQuery(id+"F2.imprint","IMPRINT",FACE,{"disambiguationData":[TD([[makeQuery(id+"F2.imprint","IMPRINT",EDGE,{"derivedFrom":sQuery(id+"F2.wireOp",EDGE,"E172")}),1.0]])]});
            var Q1;
            Q1=makeQuery(id+"F2.imprint","IMPRINT",FACE,{"disambiguationData":[TD([[makeQuery(id+"F2.imprint","IMPRINT",EDGE,{"derivedFrom":sQuery(id+"F2.wireOp",EDGE,"E176")}),1.0]])]});
            var Q2;
            Q2=makeQuery(id+"F2.imprint","IMPRINT",FACE,{"disambiguationData":[TD([[makeQuery(id+"F2.imprint","IMPRINT",EDGE,{"derivedFrom":sQuery(id+"F2.wireOp",EDGE,"E168")}),-1.0]])]});
            extrude(context, id + "F8", {"entities" : qUnion([Q0, Q1, Q2]), "operationType" : NewBodyOperationType.ADD, "depth" : 8.5 * mm});
        }
        {
            var Q0;
            Q0=makeQuery(id+"F1.opExtrude","CAP_FACE",FACE,{"disambiguationData":[OSD([sQuery(id+"F0.wireOp",EDGE,"E33"),sQuery(id+"F0.wireOp",EDGE,"E36"),sQuery(id+"F0.wireOp",EDGE,"E37"),sQuery(id+"F0.wireOp",EDGE,"E38"),sQuery(id+"F0.wireOp",EDGE,"E39"),sQuery(id+"F0.wireOp",EDGE,"E40"),sQuery(id+"F0.wireOp",EDGE,"E41"),sQuery(id+"F0.wireOp",EDGE,"E42"),sQuery(id+"F0.wireOp",EDGE,"E43"),sQuery(id+"F0.wireOp",EDGE,"E44"),sQuery(id+"F0.wireOp",EDGE,"E46"),sQuery(id+"F0.wireOp",EDGE,"E49"),sQuery(id+"F0.wireOp",EDGE,"E50")])],"isStart":true});
            var sketch = newSketch(context, id + "F9", { "sketchPlane" : qUnion([Q0])});
            skLineSegment(sketch, "E215", {"start": v(72, 22.58) * mm, "end": v(84.12, 22.58) * mm});
            skLineSegment(sketch, "E216", {"start": v(84.12, 22.58) * mm, "end": v(84.12, -20.6) * mm});
            skLineSegment(sketch, "E217", {"start": v(84.12, -20.6) * mm, "end": v(72, -20.6) * mm});
            skLineSegment(sketch, "E218", {"start": v(-67.87, -35.05) * mm, "end": v(-67.87, -31.5) * mm});
            skLineSegment(sketch, "E219", {"start": v(-65.33, -35.05) * mm, "end": v(-65.33, -31.5) * mm});
            skLineSegment(sketch, "E220", {"start": v(-62.79, -35.05) * mm, "end": v(-62.79, -31.5) * mm});
            skLineSegment(sketch, "E221", {"start": v(-60.25, -50.3) * mm, "end": v(-60.25, -49.02) * mm});
            skLineSegment(sketch, "E222", {"start": v(-60.25, -49.02) * mm, "end": v(-61.52, -49.02) * mm});
            skLineSegment(sketch, "E223", {"start": v(-61.52, -49.02) * mm, "end": v(-61.52, -46.48) * mm});
            skLineSegment(sketch, "E224", {"start": v(-61.52, -46.48) * mm, "end": v(-60.25, -46.48) * mm});
            skLineSegment(sketch, "E225", {"start": v(-60.25, -46.48) * mm, "end": v(-60.25, -35.05) * mm});
            skLineSegment(sketch, "E226", {"start": v(-60.25, -35.05) * mm, "end": v(-70.4, -35.05) * mm});
            skLineSegment(sketch, "E227", {"start": v(-70.4, -35.05) * mm, "end": v(-70.4, -46.48) * mm});
            skLineSegment(sketch, "E228", {"start": v(-70.4, -46.48) * mm, "end": v(-69.14, -46.48) * mm});
            skLineSegment(sketch, "E229", {"start": v(-69.14, -46.48) * mm, "end": v(-69.14, -49.02) * mm});
            skLineSegment(sketch, "E230", {"start": v(-69.14, -49.02) * mm, "end": v(-70.4, -49.02) * mm});
            skLineSegment(sketch, "E231", {"start": v(-70.4, -49.02) * mm, "end": v(-70.4, -50.3) * mm});
            skLineSegment(sketch, "E232", {"start": v(-70.4, -50.3) * mm, "end": v(-60.25, -50.3) * mm});
            skLineSegment(sketch, "E233", {"start": v(-5.44, 7.4) * mm, "end": v(-5.44, 7.11) * mm});
            skLineSegment(sketch, "E234", {"start": v(-5.44, 7.11) * mm, "end": v(-5.38, 6.88) * mm});
            skLineSegment(sketch, "E235", {"start": v(-5.38, 6.88) * mm, "end": v(-5.28, 6.63) * mm});
            skLineSegment(sketch, "E236", {"start": v(-5.28, 6.63) * mm, "end": v(-5.18, 6.38) * mm});
            skLineSegment(sketch, "E237", {"start": v(-5.18, 6.38) * mm, "end": v(-5.03, 6.17) * mm});
            skLineSegment(sketch, "E238", {"start": v(-5.03, 6.17) * mm, "end": v(-4.85, 5.97) * mm});
            skLineSegment(sketch, "E239", {"start": v(-2.03, 5.97) * mm, "end": v(-1.85, 6.17) * mm});
            skLineSegment(sketch, "E240", {"start": v(-1.85, 6.17) * mm, "end": v(-1.7, 6.38) * mm});
            skLineSegment(sketch, "E241", {"start": v(-1.7, 6.38) * mm, "end": v(-1.6, 6.63) * mm});
            skLineSegment(sketch, "E242", {"start": v(-1.6, 6.63) * mm, "end": v(-1.52, 6.88) * mm});
            skLineSegment(sketch, "E243", {"start": v(-1.52, 6.88) * mm, "end": v(-1.47, 7.11) * mm});
            skLineSegment(sketch, "E244", {"start": v(-1.47, 7.11) * mm, "end": v(-1.45, 7.4) * mm});
            skLineSegment(sketch, "E245", {"start": v(-1.45, 14.1) * mm, "end": v(-1.47, 14.35) * mm});
            skLineSegment(sketch, "E246", {"start": v(-1.47, 14.35) * mm, "end": v(-1.52, 14.6) * mm});
            skLineSegment(sketch, "E247", {"start": v(-1.52, 14.6) * mm, "end": v(-1.6, 14.86) * mm});
            skLineSegment(sketch, "E248", {"start": v(-1.6, 14.86) * mm, "end": v(-1.7, 15.09) * mm});
            skLineSegment(sketch, "E249", {"start": v(-1.7, 15.09) * mm, "end": v(-1.85, 15.32) * mm});
            skLineSegment(sketch, "E250", {"start": v(-1.85, 15.32) * mm, "end": v(-2.03, 15.5) * mm});
            skLineSegment(sketch, "E251", {"start": v(-4.85, 15.5) * mm, "end": v(-5.03, 15.32) * mm});
            skLineSegment(sketch, "E252", {"start": v(-5.03, 15.32) * mm, "end": v(-5.18, 15.09) * mm});
            skLineSegment(sketch, "E253", {"start": v(-5.18, 15.09) * mm, "end": v(-5.28, 14.86) * mm});
            skLineSegment(sketch, "E254", {"start": v(-5.28, 14.86) * mm, "end": v(-5.38, 14.6) * mm});
            skLineSegment(sketch, "E255", {"start": v(-5.38, 14.6) * mm, "end": v(-5.44, 14.35) * mm});
            skLineSegment(sketch, "E256", {"start": v(-5.44, 14.35) * mm, "end": v(-5.44, 14.1) * mm});
            skLineSegment(sketch, "E257", {"start": v(-72.11, -0.3) * mm, "end": v(-72.14, -0.05) * mm});
            skLineSegment(sketch, "E258", {"start": v(-72.14, -0.05) * mm, "end": v(-72.14, 0.2) * mm});
            skLineSegment(sketch, "E259", {"start": v(-72.14, 0.2) * mm, "end": v(-72.16, 0.46) * mm});
            skLineSegment(sketch, "E260", {"start": v(-72.16, 0.46) * mm, "end": v(-72.19, 0.71) * mm});
            skLineSegment(sketch, "E261", {"start": v(-72.19, 0.71) * mm, "end": v(-72.24, 0.94) * mm});
            skLineSegment(sketch, "E262", {"start": v(-72.24, 0.94) * mm, "end": v(-72.29, 1.22) * mm});
            skLineSegment(sketch, "E263", {"start": v(-72.29, 1.22) * mm, "end": v(-72.36, 1.45) * mm});
            skLineSegment(sketch, "E264", {"start": v(-72.36, 1.45) * mm, "end": v(-72.42, 1.7) * mm});
            skLineSegment(sketch, "E265", {"start": v(-72.42, 1.7) * mm, "end": v(-72.52, 1.93) * mm});
            skLineSegment(sketch, "E266", {"start": v(-72.52, 1.93) * mm, "end": v(-72.6, 2.16) * mm});
            skLineSegment(sketch, "E267", {"start": v(-72.6, 2.16) * mm, "end": v(-72.72, 2.39) * mm});
            skLineSegment(sketch, "E268", {"start": v(-72.72, 2.39) * mm, "end": v(-72.82, 2.62) * mm});
            skLineSegment(sketch, "E269", {"start": v(-72.82, 2.62) * mm, "end": v(-72.95, 2.84) * mm});
            skLineSegment(sketch, "E270", {"start": v(-72.95, 2.84) * mm, "end": v(-73.05, 3.07) * mm});
            skLineSegment(sketch, "E271", {"start": v(-73.05, 3.07) * mm, "end": v(-73.2, 3.3) * mm});
            skLineSegment(sketch, "E272", {"start": v(-73.2, 3.3) * mm, "end": v(-73.36, 3.48) * mm});
            skLineSegment(sketch, "E273", {"start": v(-73.36, 3.48) * mm, "end": v(-73.5, 3.7) * mm});
            skLineSegment(sketch, "E274", {"start": v(-73.5, 3.7) * mm, "end": v(-73.66, 3.89) * mm});
            skLineSegment(sketch, "E275", {"start": v(-73.66, 3.89) * mm, "end": v(-73.81, 4.09) * mm});
            skLineSegment(sketch, "E276", {"start": v(-73.81, 4.09) * mm, "end": v(-74, 4.27) * mm});
            skLineSegment(sketch, "E277", {"start": v(-74, 4.27) * mm, "end": v(-74.17, 4.45) * mm});
            skLineSegment(sketch, "E278", {"start": v(-74.17, 4.45) * mm, "end": v(-74.37, 4.62) * mm});
            skLineSegment(sketch, "E279", {"start": v(-74.37, 4.62) * mm, "end": v(-74.55, 4.78) * mm});
            skLineSegment(sketch, "E280", {"start": v(-74.55, 4.78) * mm, "end": v(-74.78, 4.93) * mm});
            skLineSegment(sketch, "E281", {"start": v(-74.78, 4.93) * mm, "end": v(-74.96, 5.08) * mm});
            skLineSegment(sketch, "E282", {"start": v(-74.96, 5.08) * mm, "end": v(-75.18, 5.2) * mm});
            skLineSegment(sketch, "E283", {"start": v(-75.18, 5.2) * mm, "end": v(-75.41, 5.33) * mm});
            skLineSegment(sketch, "E284", {"start": v(-75.41, 5.33) * mm, "end": v(-75.62, 5.46) * mm});
            skLineSegment(sketch, "E285", {"start": v(-75.62, 5.46) * mm, "end": v(-75.84, 5.59) * mm});
            skLineSegment(sketch, "E286", {"start": v(-75.84, 5.59) * mm, "end": v(-76.07, 5.66) * mm});
            skLineSegment(sketch, "E287", {"start": v(-76.07, 5.66) * mm, "end": v(-76.33, 5.8) * mm});
            skLineSegment(sketch, "E288", {"start": v(-76.33, 5.8) * mm, "end": v(-76.56, 5.87) * mm});
            skLineSegment(sketch, "E289", {"start": v(-76.56, 5.87) * mm, "end": v(-76.8, 5.94) * mm});
            skLineSegment(sketch, "E290", {"start": v(-76.8, 5.94) * mm, "end": v(-77.04, 6.02) * mm});
            skLineSegment(sketch, "E291", {"start": v(-77.04, 6.02) * mm, "end": v(-77.3, 6.07) * mm});
            skLineSegment(sketch, "E292", {"start": v(-77.3, 6.07) * mm, "end": v(-77.55, 6.12) * mm});
            skLineSegment(sketch, "E293", {"start": v(-77.55, 6.12) * mm, "end": v(-77.8, 6.15) * mm});
            skLineSegment(sketch, "E294", {"start": v(-77.8, 6.15) * mm, "end": v(-78.05, 6.17) * mm});
            skLineSegment(sketch, "E295", {"start": v(-78.05, 6.17) * mm, "end": v(-78.3, 6.2) * mm});
            skLineSegment(sketch, "E296", {"start": v(-78.3, 6.2) * mm, "end": v(-78.54, 6.2) * mm});
            skLineSegment(sketch, "E297", {"start": v(-78.54, 6.2) * mm, "end": v(-78.82, 6.2) * mm});
            skLineSegment(sketch, "E298", {"start": v(-78.82, 6.2) * mm, "end": v(-79.07, 6.2) * mm});
            skLineSegment(sketch, "E299", {"start": v(-79.07, 6.2) * mm, "end": v(-79.3, 6.15) * mm});
            skLineSegment(sketch, "E300", {"start": v(-79.3, 6.15) * mm, "end": v(-79.58, 6.15) * mm});
            skLineSegment(sketch, "E301", {"start": v(-79.58, 6.15) * mm, "end": v(-79.8, 6.07) * mm});
            skLineSegment(sketch, "E302", {"start": v(-79.8, 6.07) * mm, "end": v(-80.06, 6.02) * mm});
            skLineSegment(sketch, "E303", {"start": v(-80.06, 6.02) * mm, "end": v(-80.31, 5.97) * mm});
            skLineSegment(sketch, "E304", {"start": v(-80.31, 5.97) * mm, "end": v(-80.57, 5.92) * mm});
            skLineSegment(sketch, "E305", {"start": v(-80.57, 5.92) * mm, "end": v(-80.8, 5.82) * mm});
            skLineSegment(sketch, "E306", {"start": v(-80.8, 5.82) * mm, "end": v(-81.03, 5.74) * mm});
            skLineSegment(sketch, "E307", {"start": v(-81.03, 5.74) * mm, "end": v(-81.25, 5.64) * mm});
            skLineSegment(sketch, "E308", {"start": v(-81.25, 5.64) * mm, "end": v(-81.48, 5.54) * mm});
            skLineSegment(sketch, "E309", {"start": v(-81.48, 5.54) * mm, "end": v(-81.71, 5.41) * mm});
            skLineSegment(sketch, "E310", {"start": v(-81.71, 5.41) * mm, "end": v(-81.94, 5.28) * mm});
            skLineSegment(sketch, "E311", {"start": v(-81.94, 5.28) * mm, "end": v(-82.14, 5.16) * mm});
            skLineSegment(sketch, "E312", {"start": v(-82.14, 5.16) * mm, "end": v(-82.35, 5) * mm});
            skLineSegment(sketch, "E313", {"start": v(-82.35, 5) * mm, "end": v(-82.58, 4.88) * mm});
            skLineSegment(sketch, "E314", {"start": v(-82.58, 4.88) * mm, "end": v(-82.75, 4.7) * mm});
            skLineSegment(sketch, "E315", {"start": v(-82.75, 4.7) * mm, "end": v(-82.96, 4.52) * mm});
            skLineSegment(sketch, "E316", {"start": v(-82.96, 4.52) * mm, "end": v(-83.16, 4.34) * mm});
            skLineSegment(sketch, "E317", {"start": v(-83.16, 4.34) * mm, "end": v(-83.34, 4.17) * mm});
            skLineSegment(sketch, "E318", {"start": v(-83.34, 4.17) * mm, "end": v(-83.49, 4.01) * mm});
            skLineSegment(sketch, "E319", {"start": v(-83.49, 4.01) * mm, "end": v(-83.67, 3.8) * mm});
            skLineSegment(sketch, "E320", {"start": v(-83.67, 3.8) * mm, "end": v(-83.82, 3.6) * mm});
            skLineSegment(sketch, "E321", {"start": v(-83.82, 3.6) * mm, "end": v(-83.97, 3.4) * mm});
            skLineSegment(sketch, "E322", {"start": v(-83.97, 3.4) * mm, "end": v(-84.1, 3.2) * mm});
            skLineSegment(sketch, "E323", {"start": v(-84.1, 3.2) * mm, "end": v(-84.23, 2.97) * mm});
            skLineSegment(sketch, "E324", {"start": v(-84.23, 2.97) * mm, "end": v(-84.35, 2.74) * mm});
            skLineSegment(sketch, "E325", {"start": v(-84.35, 2.74) * mm, "end": v(-84.48, 2.51) * mm});
            skLineSegment(sketch, "E326", {"start": v(-84.48, 2.51) * mm, "end": v(-84.58, 2.29) * mm});
            skLineSegment(sketch, "E327", {"start": v(-84.58, 2.29) * mm, "end": v(-84.66, 2.06) * mm});
            skLineSegment(sketch, "E328", {"start": v(-84.66, 2.06) * mm, "end": v(-84.76, 1.8) * mm});
            skLineSegment(sketch, "E329", {"start": v(-84.76, 1.8) * mm, "end": v(-84.84, 1.57) * mm});
            skLineSegment(sketch, "E330", {"start": v(-84.84, 1.57) * mm, "end": v(-84.91, 1.35) * mm});
            skLineSegment(sketch, "E331", {"start": v(-84.91, 1.35) * mm, "end": v(-84.96, 1.1) * mm});
            skLineSegment(sketch, "E332", {"start": v(-84.96, 1.1) * mm, "end": v(-85.01, 0.84) * mm});
            skLineSegment(sketch, "E333", {"start": v(-85.01, 0.84) * mm, "end": v(-85.06, 0.58) * mm});
            skLineSegment(sketch, "E334", {"start": v(-85.06, 0.58) * mm, "end": v(-85.1, 0.33) * mm});
            skLineSegment(sketch, "E335", {"start": v(-85.1, 0.33) * mm, "end": v(-85.12, 0.08) * mm});
            skLineSegment(sketch, "E336", {"start": v(-85.12, 0.08) * mm, "end": v(-85.12, -0.18) * mm});
            skLineSegment(sketch, "E337", {"start": v(-85.12, -0.18) * mm, "end": v(-85.12, -0.43) * mm});
            skLineSegment(sketch, "E338", {"start": v(-85.12, -0.43) * mm, "end": v(-85.12, -0.69) * mm});
            skLineSegment(sketch, "E339", {"start": v(-85.12, -0.69) * mm, "end": v(-85.1, -0.94) * mm});
            skLineSegment(sketch, "E340", {"start": v(-85.1, -0.94) * mm, "end": v(-85.06, -1.2) * mm});
            skLineSegment(sketch, "E341", {"start": v(-85.06, -1.2) * mm, "end": v(-85.01, -1.42) * mm});
            skLineSegment(sketch, "E342", {"start": v(-85.01, -1.42) * mm, "end": v(-84.96, -1.68) * mm});
            skLineSegment(sketch, "E343", {"start": v(-84.96, -1.68) * mm, "end": v(-84.91, -1.93) * mm});
            skLineSegment(sketch, "E344", {"start": v(-84.91, -1.93) * mm, "end": v(-84.84, -2.18) * mm});
            skLineSegment(sketch, "E345", {"start": v(-84.84, -2.18) * mm, "end": v(-84.76, -2.41) * mm});
            skLineSegment(sketch, "E346", {"start": v(-84.76, -2.41) * mm, "end": v(-84.66, -2.64) * mm});
            skLineSegment(sketch, "E347", {"start": v(-84.66, -2.64) * mm, "end": v(-84.58, -2.9) * mm});
            skLineSegment(sketch, "E348", {"start": v(-84.58, -2.9) * mm, "end": v(-84.48, -3.12) * mm});
            skLineSegment(sketch, "E349", {"start": v(-84.48, -3.12) * mm, "end": v(-84.35, -3.35) * mm});
            skLineSegment(sketch, "E350", {"start": v(-84.35, -3.35) * mm, "end": v(-84.23, -3.56) * mm});
            skLineSegment(sketch, "E351", {"start": v(-84.23, -3.56) * mm, "end": v(-84.1, -3.78) * mm});
            skLineSegment(sketch, "E352", {"start": v(-84.1, -3.78) * mm, "end": v(-83.97, -3.99) * mm});
            skLineSegment(sketch, "E353", {"start": v(-83.97, -3.99) * mm, "end": v(-83.82, -4.2) * mm});
            skLineSegment(sketch, "E354", {"start": v(-83.82, -4.2) * mm, "end": v(-83.67, -4.4) * mm});
            skLineSegment(sketch, "E355", {"start": v(-83.67, -4.4) * mm, "end": v(-83.49, -4.6) * mm});
            skLineSegment(sketch, "E356", {"start": v(-83.49, -4.6) * mm, "end": v(-83.34, -4.78) * mm});
            skLineSegment(sketch, "E357", {"start": v(-83.34, -4.78) * mm, "end": v(-83.16, -4.95) * mm});
            skLineSegment(sketch, "E358", {"start": v(-83.16, -4.95) * mm, "end": v(-82.96, -5.13) * mm});
            skLineSegment(sketch, "E359", {"start": v(-82.96, -5.13) * mm, "end": v(-82.75, -5.3) * mm});
            skLineSegment(sketch, "E360", {"start": v(-82.75, -5.3) * mm, "end": v(-82.58, -5.46) * mm});
            skLineSegment(sketch, "E361", {"start": v(-82.58, -5.46) * mm, "end": v(-82.35, -5.61) * mm});
            skLineSegment(sketch, "E362", {"start": v(-82.35, -5.61) * mm, "end": v(-82.17, -5.74) * mm});
            skLineSegment(sketch, "E363", {"start": v(-82.17, -5.74) * mm, "end": v(-81.94, -5.9) * mm});
            skLineSegment(sketch, "E364", {"start": v(-81.94, -5.9) * mm, "end": v(-81.71, -6.02) * mm});
            skLineSegment(sketch, "E365", {"start": v(-81.71, -6.02) * mm, "end": v(-81.48, -6.12) * mm});
            skLineSegment(sketch, "E366", {"start": v(-81.48, -6.12) * mm, "end": v(-81.25, -6.22) * mm});
            skLineSegment(sketch, "E367", {"start": v(-81.25, -6.22) * mm, "end": v(-81.03, -6.32) * mm});
            skLineSegment(sketch, "E368", {"start": v(-81.03, -6.32) * mm, "end": v(-80.8, -6.43) * mm});
            skLineSegment(sketch, "E369", {"start": v(-80.8, -6.43) * mm, "end": v(-80.57, -6.5) * mm});
            skLineSegment(sketch, "E370", {"start": v(-80.57, -6.5) * mm, "end": v(-80.31, -6.58) * mm});
            skLineSegment(sketch, "E371", {"start": v(-80.31, -6.58) * mm, "end": v(-80.06, -6.63) * mm});
            skLineSegment(sketch, "E372", {"start": v(-80.06, -6.63) * mm, "end": v(-79.8, -6.68) * mm});
            skLineSegment(sketch, "E373", {"start": v(-79.8, -6.68) * mm, "end": v(-79.58, -6.73) * mm});
            skLineSegment(sketch, "E374", {"start": v(-79.58, -6.73) * mm, "end": v(-79.3, -6.76) * mm});
            skLineSegment(sketch, "E375", {"start": v(-79.3, -6.76) * mm, "end": v(-79.07, -6.78) * mm});
            skLineSegment(sketch, "E376", {"start": v(-79.07, -6.78) * mm, "end": v(-78.82, -6.78) * mm});
            skLineSegment(sketch, "E377", {"start": v(-78.82, -6.78) * mm, "end": v(-78.54, -6.78) * mm});
            skLineSegment(sketch, "E378", {"start": v(-78.54, -6.78) * mm, "end": v(-78.3, -6.78) * mm});
            skLineSegment(sketch, "E379", {"start": v(-78.3, -6.78) * mm, "end": v(-78.05, -6.78) * mm});
            skLineSegment(sketch, "E380", {"start": v(-78.05, -6.78) * mm, "end": v(-77.8, -6.76) * mm});
            skLineSegment(sketch, "E381", {"start": v(-77.8, -6.76) * mm, "end": v(-77.55, -6.7) * mm});
            skLineSegment(sketch, "E382", {"start": v(-77.55, -6.7) * mm, "end": v(-77.3, -6.68) * mm});
            skLineSegment(sketch, "E383", {"start": v(-77.3, -6.68) * mm, "end": v(-77.04, -6.6) * mm});
            skLineSegment(sketch, "E384", {"start": v(-77.04, -6.6) * mm, "end": v(-76.8, -6.55) * mm});
            skLineSegment(sketch, "E385", {"start": v(-76.8, -6.55) * mm, "end": v(-76.56, -6.48) * mm});
            skLineSegment(sketch, "E386", {"start": v(-76.56, -6.48) * mm, "end": v(-76.33, -6.4) * mm});
            skLineSegment(sketch, "E387", {"start": v(-76.33, -6.4) * mm, "end": v(-76.07, -6.27) * mm});
            skLineSegment(sketch, "E388", {"start": v(-76.07, -6.27) * mm, "end": v(-75.84, -6.17) * mm});
            skLineSegment(sketch, "E389", {"start": v(-75.84, -6.17) * mm, "end": v(-75.62, -6.07) * mm});
            skLineSegment(sketch, "E390", {"start": v(-75.62, -6.07) * mm, "end": v(-75.41, -5.94) * mm});
            skLineSegment(sketch, "E391", {"start": v(-75.41, -5.94) * mm, "end": v(-75.18, -5.82) * mm});
            skLineSegment(sketch, "E392", {"start": v(-75.18, -5.82) * mm, "end": v(-74.96, -5.69) * mm});
            skLineSegment(sketch, "E393", {"start": v(-74.96, -5.69) * mm, "end": v(-74.78, -5.54) * mm});
            skLineSegment(sketch, "E394", {"start": v(-74.78, -5.54) * mm, "end": v(-74.55, -5.38) * mm});
            skLineSegment(sketch, "E395", {"start": v(-74.55, -5.38) * mm, "end": v(-74.37, -5.23) * mm});
            skLineSegment(sketch, "E396", {"start": v(-74.37, -5.23) * mm, "end": v(-74.17, -5.05) * mm});
            skLineSegment(sketch, "E397", {"start": v(-74.17, -5.05) * mm, "end": v(-74, -4.88) * mm});
            skLineSegment(sketch, "E398", {"start": v(-74, -4.88) * mm, "end": v(-73.81, -4.7) * mm});
            skLineSegment(sketch, "E399", {"start": v(-73.81, -4.7) * mm, "end": v(-73.66, -4.5) * mm});
            skLineSegment(sketch, "E400", {"start": v(-73.66, -4.5) * mm, "end": v(-73.5, -4.32) * mm});
            skLineSegment(sketch, "E401", {"start": v(-73.5, -4.32) * mm, "end": v(-73.36, -4.09) * mm});
            skLineSegment(sketch, "E402", {"start": v(-73.36, -4.09) * mm, "end": v(-73.2, -3.91) * mm});
            skLineSegment(sketch, "E403", {"start": v(-73.2, -3.91) * mm, "end": v(-73.05, -3.68) * mm});
            skLineSegment(sketch, "E404", {"start": v(-73.05, -3.68) * mm, "end": v(-72.95, -3.45) * mm});
            skLineSegment(sketch, "E405", {"start": v(-72.95, -3.45) * mm, "end": v(-72.82, -3.23) * mm});
            skLineSegment(sketch, "E406", {"start": v(-72.82, -3.23) * mm, "end": v(-72.72, -3) * mm});
            skLineSegment(sketch, "E407", {"start": v(-72.72, -3) * mm, "end": v(-72.6, -2.77) * mm});
            skLineSegment(sketch, "E408", {"start": v(-72.6, -2.77) * mm, "end": v(-72.52, -2.54) * mm});
            skLineSegment(sketch, "E409", {"start": v(-72.52, -2.54) * mm, "end": v(-72.42, -2.29) * mm});
            skLineSegment(sketch, "E410", {"start": v(-72.42, -2.29) * mm, "end": v(-72.36, -2.06) * mm});
            skLineSegment(sketch, "E411", {"start": v(-72.36, -2.06) * mm, "end": v(-72.29, -1.8) * mm});
            skLineSegment(sketch, "E412", {"start": v(-72.29, -1.8) * mm, "end": v(-72.24, -1.55) * mm});
            skLineSegment(sketch, "E413", {"start": v(-72.24, -1.55) * mm, "end": v(-72.19, -1.3) * mm});
            skLineSegment(sketch, "E414", {"start": v(-72.19, -1.3) * mm, "end": v(-72.16, -1.07) * mm});
            skLineSegment(sketch, "E415", {"start": v(-72.16, -1.07) * mm, "end": v(-72.14, -0.81) * mm});
            skLineSegment(sketch, "E416", {"start": v(-72.14, -0.81) * mm, "end": v(-72.14, -0.56) * mm});
            skLineSegment(sketch, "E417", {"start": v(-72.14, -0.56) * mm, "end": v(-72.11, -0.3) * mm});
            skLineSegment(sketch, "E418", {"start": v(-71.25, -48.46) * mm, "end": v(-71.25, -31.14) * mm});
            skLineSegment(sketch, "E419", {"start": v(-88.54, -48.46) * mm, "end": v(-88.54, -31.14) * mm});
            skLineSegment(sketch, "E420", {"start": v(-88.54, -48.46) * mm, "end": v(-81.89, -48.46) * mm});
            skLineSegment(sketch, "E421", {"start": v(-77.9, -48.46) * mm, "end": v(-71.25, -48.46) * mm});
            skLineSegment(sketch, "E422", {"start": v(-77.9, -31.14) * mm, "end": v(-71.25, -31.14) * mm});
            skLineSegment(sketch, "E423", {"start": v(-88.54, -31.14) * mm, "end": v(-81.89, -31.14) * mm});
            skLineSegment(sketch, "E424", {"start": v(36.65, -50.55) * mm, "end": v(44.7, -50.55) * mm});
            skLineSegment(sketch, "E425", {"start": v(36.65, -65.02) * mm, "end": v(44.7, -65.02) * mm});
            skLineSegment(sketch, "E426", {"start": v(36.65, -65.02) * mm, "end": v(36.65, -50.55) * mm});
            skLineSegment(sketch, "E427", {"start": v(44.7, -65.02) * mm, "end": v(44.7, -50.55) * mm});
            skLineSegment(sketch, "E428", {"start": v(-1.45, 7.4) * mm, "end": v(-1.45, 14.1) * mm});
            skLineSegment(sketch, "E429", {"start": v(-5.44, 7.4) * mm, "end": v(-5.44, 14.1) * mm});
            skLineSegment(sketch, "E430", {"start": v(6.07, -24.9) * mm, "end": v(14.1, -24.9) * mm});
            skLineSegment(sketch, "E431", {"start": v(6.07, -10.41) * mm, "end": v(14.1, -10.41) * mm});
            skLineSegment(sketch, "E432", {"start": v(14.1, -24.9) * mm, "end": v(14.1, -10.41) * mm});
            skLineSegment(sketch, "E433", {"start": v(6.07, -24.9) * mm, "end": v(6.07, -10.41) * mm});
            skLineSegment(sketch, "E434", {"start": v(18.26, -24.9) * mm, "end": v(26.34, -24.9) * mm});
            skLineSegment(sketch, "E435", {"start": v(18.26, -10.41) * mm, "end": v(26.34, -10.41) * mm});
            skLineSegment(sketch, "E436", {"start": v(26.34, -24.9) * mm, "end": v(26.34, -10.41) * mm});
            skLineSegment(sketch, "E437", {"start": v(18.26, -24.9) * mm, "end": v(18.26, -10.41) * mm});
            skLineSegment(sketch, "E438", {"start": v(19.81, -50.67) * mm, "end": v(19.81, -36.17) * mm});
            skLineSegment(sketch, "E439", {"start": v(11.76, -50.67) * mm, "end": v(11.76, -36.17) * mm});
            skLineSegment(sketch, "E440", {"start": v(11.76, -50.67) * mm, "end": v(19.81, -50.67) * mm});
            skLineSegment(sketch, "E441", {"start": v(11.76, -36.17) * mm, "end": v(19.81, -36.17) * mm});
            skLineSegment(sketch, "E442", {"start": v(23.44, -36.17) * mm, "end": v(31.47, -36.17) * mm});
            skLineSegment(sketch, "E443", {"start": v(23.44, -50.67) * mm, "end": v(31.47, -50.67) * mm});
            skLineSegment(sketch, "E444", {"start": v(23.44, -50.67) * mm, "end": v(23.44, -36.17) * mm});
            skLineSegment(sketch, "E445", {"start": v(31.47, -50.67) * mm, "end": v(31.47, -36.17) * mm});
            skLineSegment(sketch, "E446", {"start": v(51.38, -36.17) * mm, "end": v(59.41, -36.17) * mm});
            skLineSegment(sketch, "E447", {"start": v(51.38, -50.67) * mm, "end": v(59.41, -50.67) * mm});
            skLineSegment(sketch, "E448", {"start": v(51.38, -50.67) * mm, "end": v(51.38, -36.17) * mm});
            skLineSegment(sketch, "E449", {"start": v(59.41, -50.67) * mm, "end": v(59.41, -36.17) * mm});
            skLineSegment(sketch, "E450", {"start": v(64.08, -36.17) * mm, "end": v(72.11, -36.17) * mm});
            skLineSegment(sketch, "E451", {"start": v(64.08, -50.67) * mm, "end": v(72.11, -50.67) * mm});
            skLineSegment(sketch, "E452", {"start": v(64.08, -50.67) * mm, "end": v(64.08, -36.17) * mm});
            skLineSegment(sketch, "E453", {"start": v(72.11, -50.67) * mm, "end": v(72.11, -36.17) * mm});
            skLineSegment(sketch, "E454", {"start": v(76.78, -36.17) * mm, "end": v(84.84, -36.17) * mm});
            skLineSegment(sketch, "E455", {"start": v(76.78, -50.67) * mm, "end": v(84.84, -50.67) * mm});
            skLineSegment(sketch, "E456", {"start": v(76.78, -50.67) * mm, "end": v(76.78, -36.17) * mm});
            skLineSegment(sketch, "E457", {"start": v(84.84, -50.67) * mm, "end": v(84.84, -36.17) * mm});
            skLineSegment(sketch, "E458", {"start": v(-92.96, -47) * mm, "end": v(-92.7, -46.96) * mm});
            skLineSegment(sketch, "E459", {"start": v(-92.7, -46.96) * mm, "end": v(-92.46, -46.91) * mm});
            skLineSegment(sketch, "E460", {"start": v(-92.46, -46.91) * mm, "end": v(-92.23, -46.81) * mm});
            skLineSegment(sketch, "E461", {"start": v(-92.23, -46.81) * mm, "end": v(-92.02, -46.69) * mm});
            skLineSegment(sketch, "E462", {"start": v(-92.02, -46.69) * mm, "end": v(-91.85, -46.5) * mm});
            skLineSegment(sketch, "E463", {"start": v(-91.85, -46.5) * mm, "end": v(-91.7, -46.33) * mm});
            skLineSegment(sketch, "E464", {"start": v(-91.7, -46.33) * mm, "end": v(-91.6, -46.1) * mm});
            skLineSegment(sketch, "E465", {"start": v(-91.6, -46.1) * mm, "end": v(-91.5, -45.87) * mm});
            skLineSegment(sketch, "E466", {"start": v(-91.5, -45.87) * mm, "end": v(-91.47, -45.62) * mm});
            skLineSegment(sketch, "E467", {"start": v(-91.47, -45.62) * mm, "end": v(-91.47, -45.36) * mm});
            skLineSegment(sketch, "E468", {"start": v(-91.47, -45.36) * mm, "end": v(-91.5, -45.14) * mm});
            skLineSegment(sketch, "E469", {"start": v(-91.5, -45.14) * mm, "end": v(-91.6, -44.88) * mm});
            skLineSegment(sketch, "E470", {"start": v(-91.6, -44.88) * mm, "end": v(-91.7, -44.68) * mm});
            skLineSegment(sketch, "E471", {"start": v(-91.7, -44.68) * mm, "end": v(-91.85, -44.5) * mm});
            skLineSegment(sketch, "E472", {"start": v(-91.85, -44.5) * mm, "end": v(-92.02, -44.32) * mm});
            skLineSegment(sketch, "E473", {"start": v(-92.02, -44.32) * mm, "end": v(-92.23, -44.17) * mm});
            skLineSegment(sketch, "E474", {"start": v(-92.23, -44.17) * mm, "end": v(-92.46, -44.1) * mm});
            skLineSegment(sketch, "E475", {"start": v(-92.46, -44.1) * mm, "end": v(-92.7, -44.02) * mm});
            skLineSegment(sketch, "E476", {"start": v(-92.7, -44.02) * mm, "end": v(-92.96, -44) * mm});
            skLineSegment(sketch, "E477", {"start": v(-92.96, 50.01) * mm, "end": v(-92.68, 50.01) * mm});
            skLineSegment(sketch, "E478", {"start": v(-92.68, 50.01) * mm, "end": v(-92.46, 50.09) * mm});
            skLineSegment(sketch, "E479", {"start": v(-92.46, 50.09) * mm, "end": v(-92.2, 50.2) * mm});
            skLineSegment(sketch, "E480", {"start": v(-92.2, 50.2) * mm, "end": v(-92, 50.37) * mm});
            skLineSegment(sketch, "E481", {"start": v(-92, 50.37) * mm, "end": v(-91.82, 50.52) * mm});
            skLineSegment(sketch, "E482", {"start": v(-91.82, 50.52) * mm, "end": v(-91.64, 50.75) * mm});
            skLineSegment(sketch, "E483", {"start": v(-91.64, 50.75) * mm, "end": v(-91.54, 50.98) * mm});
            skLineSegment(sketch, "E484", {"start": v(-91.54, 50.98) * mm, "end": v(-91.47, 51.23) * mm});
            skLineSegment(sketch, "E485", {"start": v(-91.47, 51.23) * mm, "end": v(-91.47, 51.49) * mm});
            skLineSegment(sketch, "E486", {"start": v(-91.47, 51.49) * mm, "end": v(-91.47, 51.74) * mm});
            skLineSegment(sketch, "E487", {"start": v(-91.47, 51.74) * mm, "end": v(-91.54, 52) * mm});
            skLineSegment(sketch, "E488", {"start": v(-91.54, 52) * mm, "end": v(-91.64, 52.25) * mm});
            skLineSegment(sketch, "E489", {"start": v(-91.64, 52.25) * mm, "end": v(-91.8, 52.45) * mm});
            skLineSegment(sketch, "E490", {"start": v(-91.8, 52.45) * mm, "end": v(-91.97, 52.65) * mm});
            skLineSegment(sketch, "E491", {"start": v(-91.97, 52.65) * mm, "end": v(-92.18, 52.78) * mm});
            skLineSegment(sketch, "E492", {"start": v(-92.18, 52.78) * mm, "end": v(-92.43, 52.9) * mm});
            skLineSegment(sketch, "E493", {"start": v(-92.43, 52.9) * mm, "end": v(-92.68, 52.98) * mm});
            skLineSegment(sketch, "E494", {"start": v(88.01, -37.5) * mm, "end": v(88.01, 37.5) * mm});
            skLineSegment(sketch, "E495", {"start": v(-95, -44) * mm, "end": v(-95, 50.01) * mm});
            skLineSegment(sketch, "E496", {"start": v(-95, -52) * mm, "end": v(-95, -47) * mm});
            skLineSegment(sketch, "E497", {"start": v(-95, -44) * mm, "end": v(-92.96, -44) * mm});
            skLineSegment(sketch, "E498", {"start": v(-95, -47) * mm, "end": v(-92.96, -47) * mm});
            skLineSegment(sketch, "E499", {"start": v(-95, 50.01) * mm, "end": v(-92.96, 50.01) * mm});
            skLineSegment(sketch, "E500", {"start": v(-72, 75) * mm, "end": v(72, 75) * mm});
            skLineSegment(sketch, "E501", {"start": v(-72, -75) * mm, "end": v(72, -75) * mm});
            skLineSegment(sketch, "E502", {"start": v(-95, -52) * mm, "end": v(-72, -75) * mm});
            skLineSegment(sketch, "E503", {"start": v(95, 37.5) * mm, "end": v(95, 52) * mm});
            skLineSegment(sketch, "E504", {"start": v(95, -52) * mm, "end": v(95, -37.5) * mm});
            skLineSegment(sketch, "E505", {"start": v(72, 75) * mm, "end": v(95, 52) * mm});
            skLineSegment(sketch, "E506", {"start": v(72, -75) * mm, "end": v(95, -52) * mm});
            skLineSegment(sketch, "E507", {"start": v(88.01, 37.5) * mm, "end": v(95, 37.5) * mm});
            skLineSegment(sketch, "E508", {"start": v(88.01, -37.5) * mm, "end": v(95, -37.5) * mm});
            skLineSegment(sketch, "E509", {"start": v(-93.2, 52.98) * mm, "end": v(-92.68, 52.98) * mm});
            skLineSegment(sketch, "E510", {"start": v(-94, 53) * mm, "end": v(-72, 75) * mm});
            skLineSegment(sketch, "E511", {"start": v(-94, 53) * mm, "end": v(-93.22, 53) * mm});
            skLineSegment(sketch, "E512", {"start": v(-81.89, -31.14) * mm, "end": v(-77.9, -31.14) * mm});
            skLineSegment(sketch, "E513", {"start": v(-81.89, -48.46) * mm, "end": v(-77.9, -48.46) * mm});
            skLineSegment(sketch, "E514", {"start": v(-67.87, -31.5) * mm, "end": v(-62.79, -31.5) * mm});
            skLineSegment(sketch, "E515", {"start": v(-4.85, 15.5) * mm, "end": v(-2.03, 15.5) * mm});
            skLineSegment(sketch, "E516", {"start": v(-4.85, 5.97) * mm, "end": v(-2.03, 5.97) * mm});
            skSolve(sketch);
        }
        {
            var Q0;
            Q0=makeQuery(id+"F9.imprint","IMPRINT",FACE,{"disambiguationData":[TD([[makeQuery(id+"F9.imprint","IMPRINT",EDGE,{"derivedFrom":sQuery(id+"F9.wireOp",EDGE,"E430")}),1.0]])]});
            var Q1;
            Q1=makeQuery(id+"F9.imprint","IMPRINT",FACE,{"disambiguationData":[TD([[makeQuery(id+"F9.imprint","IMPRINT",EDGE,{"derivedFrom":sQuery(id+"F9.wireOp",EDGE,"E434")}),1.0]])]});
            var Q2;
            Q2=makeQuery(id+"F9.imprint","IMPRINT",FACE,{"disambiguationData":[TD([[makeQuery(id+"F9.imprint","IMPRINT",EDGE,{"derivedFrom":sQuery(id+"F9.wireOp",EDGE,"E438")}),1.0]])]});
            var Q3;
            Q3=makeQuery(id+"F9.imprint","IMPRINT",FACE,{"disambiguationData":[TD([[makeQuery(id+"F9.imprint","IMPRINT",EDGE,{"derivedFrom":sQuery(id+"F9.wireOp",EDGE,"E442")}),-1.0]])]});
            var Q4;
            Q4=makeQuery(id+"F9.imprint","IMPRINT",FACE,{"disambiguationData":[TD([[makeQuery(id+"F9.imprint","IMPRINT",EDGE,{"derivedFrom":sQuery(id+"F9.wireOp",EDGE,"E424")}),-1.0]])]});
            var Q5;
            Q5=makeQuery(id+"F9.imprint","IMPRINT",FACE,{"disambiguationData":[TD([[makeQuery(id+"F9.imprint","IMPRINT",EDGE,{"derivedFrom":sQuery(id+"F9.wireOp",EDGE,"E446")}),-1.0]])]});
            var Q6;
            Q6=makeQuery(id+"F9.imprint","IMPRINT",FACE,{"disambiguationData":[TD([[makeQuery(id+"F9.imprint","IMPRINT",EDGE,{"derivedFrom":sQuery(id+"F9.wireOp",EDGE,"E450")}),-1.0]])]});
            var Q7;
            Q7=makeQuery(id+"F9.imprint","IMPRINT",FACE,{"disambiguationData":[TD([[makeQuery(id+"F9.imprint","IMPRINT",EDGE,{"derivedFrom":sQuery(id+"F9.wireOp",EDGE,"E454")}),-1.0]])]});
            extrude(context, id + "F10", {"entities" : qUnion([Q0, Q1, Q2, Q3, Q4, Q5, Q6, Q7]), "operationType" : NewBodyOperationType.ADD, "depth" : 8.85 * mm});
        }
        {
            var Q0;
            Q0=makeQuery(id+"F9.imprint","IMPRINT",FACE,{"disambiguationData":[TD([[makeQuery(id+"F9.imprint","IMPRINT",EDGE,{"derivedFrom":sQuery(id+"F9.wireOp",EDGE,"E418")}),1.0]])]});
            var Q1;
            Q1=makeQuery(id+"F9.imprint","IMPRINT",FACE,{"disambiguationData":[TD([[makeQuery(id+"F9.imprint","IMPRINT",EDGE,{"derivedFrom":sQuery(id+"F9.wireOp",EDGE,"E221")}),1.0]])]});
            var Q2;
            {var subQ0=sQuery(id+"F9.wireOp",EDGE,"E219");Q2=makeQuery(id+"F9.imprint","IMPRINT",FACE,{"disambiguationData":[TD([[makeQuery(id+"F9.imprint","IMPRINT",EDGE,{"derivedFrom":subQ0}),-1.0]])]});}
            var Q3;
            {var subQ0=sQuery(id+"F9.wireOp",EDGE,"E218");Q3=makeQuery(id+"F9.imprint","IMPRINT",FACE,{"disambiguationData":[TD([[makeQuery(id+"F9.imprint","IMPRINT",EDGE,{"derivedFrom":subQ0}),-1.0]])]});}
            extrude(context, id + "F11", {"entities" : qUnion([Q0, Q1, Q2, Q3]), "operationType" : NewBodyOperationType.ADD, "depth" : 5 * mm});
        }
        {
            var Q0;
            Q0=makeQuery(id+"F9.imprint","IMPRINT",FACE,{"disambiguationData":[TD([[makeQuery(id+"F9.imprint","IMPRINT",EDGE,{"derivedFrom":sQuery(id+"F9.wireOp",EDGE,"E257")}),1.0]])]});
            extrude(context, id + "F12", {"entities" : qUnion([Q0]), "operationType" : NewBodyOperationType.ADD, "depth" : 10 * mm});
        }
        {
            var Q0;
            Q0=makeQuery(id+"F9.imprint","IMPRINT",FACE,{"disambiguationData":[TD([[makeQuery(id+"F9.imprint","IMPRINT",EDGE,{"derivedFrom":sQuery(id+"F9.wireOp",EDGE,"E233")}),1.0]])]});
            extrude(context, id + "F13", {"entities" : qUnion([Q0]), "operationType" : NewBodyOperationType.ADD, "depth" : 5 * mm});
        }
    });
